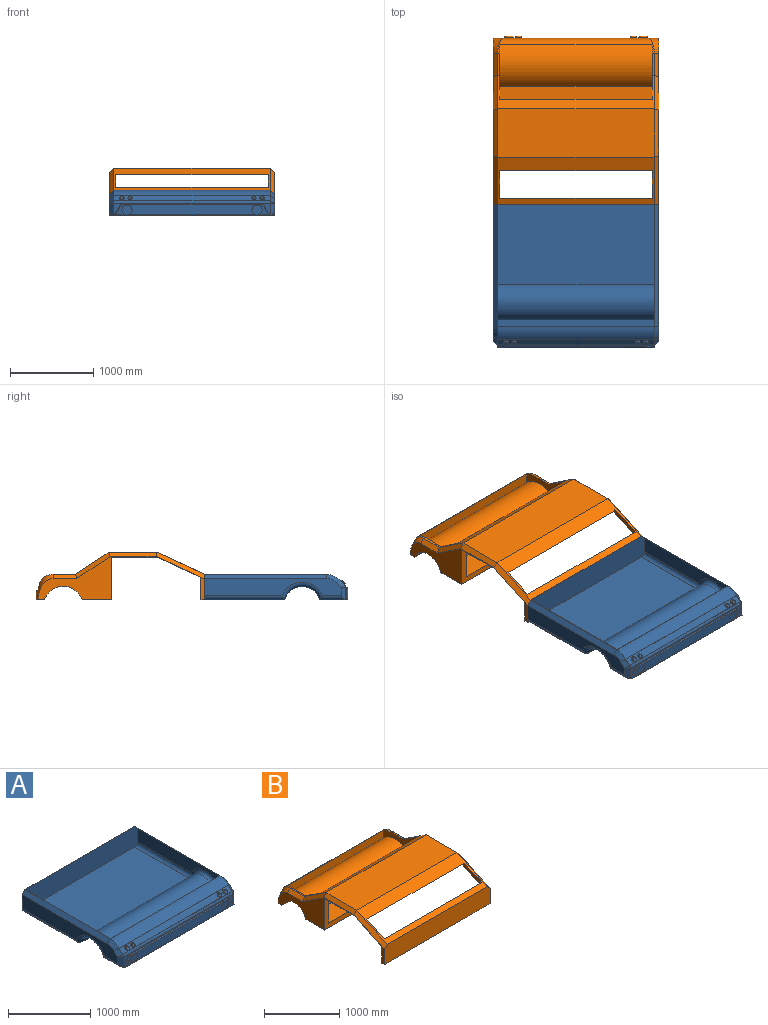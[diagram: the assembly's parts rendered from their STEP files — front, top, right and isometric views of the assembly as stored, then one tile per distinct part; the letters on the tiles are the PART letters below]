
ASSEMBLY  parts=2 mates=1
PART A: 79 faces, bbox 1981.2x1717.2x313 mm
  f0: plane 145.61x89.98mm, normal (0,-1,0), area 6551.4mm2, adj f11,f17,f63
  f1: plane 1879.6x327.04mm, normal (0,0,-1), area 614695.6mm2, adj f2,f22,f25,f63,f66,f74
  f2: cylinder r=215.54mm len=1879.6mm, axis (-1,0,0), area 1057523.4mm2, adj f1,f3,f23,f26
  f3: plane 1879.6x961.54mm, normal (0,0,-1), area 1807313.3mm2, adj f2,f4,f24,f27
  f4: plane 1981.2x306.36mm, normal (0,1,0), area 603262.1mm2, adj f3,f5,f7,f8,f16,f21,f24,f27
  f5: plane 1879.6x1462.7mm, normal (0,0,1), area 15264.3mm2, adj f4,f10,f16,f21,f32,f43,f48
  f6: plane 145.61x89.98mm, normal (0,-1,0), area 6551.4mm2, adj f11,f12,f66
  f7: plane 1641.03x204.76mm, normal (1,0,0), area 273561.9mm2, adj f4,f17,f19,f20,f21,f25,f26,f27
  f8: plane 1641.03x204.76mm, normal (-1,0,0), area 273561.9mm2, adj f4,f12,f14,f15,f16,f22,f23,f24
  f9: plane 1879.6x61.59mm, normal (0,-0.71,0.71), area 153947.2mm2, adj f10,f11,f14,f19,f55,f57,f59,f61
  f10: cylinder r=215.9mm len=1879.6mm, axis (-1,0,0), area 318719mm2, adj f5,f9,f15,f20,f28
  f11: cylinder r=50.8mm len=1879.6mm, axis (1,0,0), area 74992.7mm2, adj f0,f6,f9,f13,f18,f64
  f12: plane 145.61x50.8mm, normal (-0.71,-0.71,0), area 9677.9mm2, adj f6,f8,f13,f22
  f13: cone r=50.8mm half-angle=45deg, axis (1,0,0), area 1433.2mm2, adj f11,f12,f14
  f14: plane 97.51x97.51mm, normal (-0.71,-0.5,0.5), area 6257.1mm2, adj f8,f9,f13,f15
  f15: cone r=165.1mm half-angle=45deg, axis (1,0,0), area 10748.9mm2, adj f8,f10,f14,f16
  f16: plane 1462.7x50.8mm, normal (-0.71,0,0.71), area 105083.6mm2, adj f4,f5,f8,f15
  f17: plane 145.61x50.8mm, normal (0.71,-0.71,0), area 9677.9mm2, adj f0,f7,f18,f25
  f18: cone r=50.8mm half-angle=45deg, axis (-1,0,0), area 1433.2mm2, adj f11,f17,f19
  f19: plane 97.51x97.51mm, normal (0.71,-0.5,0.5), area 6257.1mm2, adj f7,f9,f18,f20
  f20: cone r=165.1mm half-angle=45deg, axis (-1,0,0), area 10748.9mm2, adj f7,f10,f19,f21
  f21: plane 1462.7x50.8mm, normal (0.71,0,0.71), area 105083.6mm2, adj f4,f5,f7,f20
  f22: cylinder r=50.8mm len=314.34mm, axis (0,1,0), area 21434.4mm2, adj f1,f8,f12,f23
  f23: torus R=266.34mm, axis (1,0,0), area 46455.3mm2, adj f2,f8,f22,f24
  f24: cylinder r=50.8mm len=961.54mm, axis (0,1,0), area 75659.8mm2, adj f3,f4,f8,f23
  f25: cylinder r=50.8mm len=314.34mm, axis (0,-1,0), area 21434.4mm2, adj f1,f7,f17,f26
  f26: torus R=266.34mm, axis (1,0,0), area 46455.3mm2, adj f2,f7,f25,f27
  f27: cylinder r=50.8mm len=961.54mm, axis (0,-1,0), area 75659.8mm2, adj f3,f4,f7,f26
  f28: plane 1877.5x2.54mm, normal (0,1,0), area 4762.4mm2, adj f10,f37,f43,f48
  f29: plane 1879.6x309.86mm, normal (0,0,1), area 582417.3mm2, adj f30,f33,f39,f44,f49,f52
  f30: cylinder r=218.08mm len=1879.6mm, axis (-1,0,0), area 1062679mm2, adj f29,f31,f50,f53
  f31: plane 1879.6x957.07mm, normal (0,0,1), area 1798907.1mm2, adj f30,f32,f51,f54
  f32: plane 1976.12x303.82mm, normal (0,-1,0), area 596686.5mm2, adj f5,f31,f34,f35,f43,f48,f51,f54
  f33: plane 1877.5x143.07mm, normal (0,1,0), area 268618.7mm2, adj f29,f38,f39,f44
  f34: plane 1637.44x203.7mm, normal (-1,0,0), area 271178.6mm2, adj f32,f44,f46,f47,f48,f52,f53,f54
  f35: plane 1637.44x203.7mm, normal (1,0,0), area 271178.6mm2, adj f32,f39,f41,f42,f43,f49,f50,f51
  f36: plane 1877.5x61.59mm, normal (0,0.71,-0.71), area 163520.3mm2, adj f37,f38,f41,f46
  f37: cylinder r=213.36mm len=1877.5mm, axis (-1,0,0), area 314616.8mm2, adj f28,f36,f42,f47
  f38: cylinder r=48.26mm len=1877.5mm, axis (1,0,0), area 71163.3mm2, adj f33,f36,f40,f45
  f39: plane 143.07x49.31mm, normal (0.71,0.71,0), area 9270.4mm2, adj f29,f33,f35,f40,f41,f49
  f40: cone r=49mm half-angle=45deg, axis (1,0,0), area 1293.4mm2, adj f38,f39,f41
  f41: plane 96.45x96.15mm, normal (0.71,0.5,-0.5), area 6073.5mm2, adj f35,f36,f39,f40,f42
  f42: cone r=163.3mm half-angle=45deg, axis (1,0,0), area 10335.7mm2, adj f35,f37,f41,f43
  f43: plane 1460.16x51.85mm, normal (0.71,0,-0.71), area 107073.7mm2, adj f5,f28,f32,f35,f42
  f44: plane 143.07x49.31mm, normal (-0.71,0.71,0), area 9270.4mm2, adj f29,f33,f34,f45,f46,f52
  f45: cone r=49mm half-angle=45deg, axis (-1,0,0), area 1293.4mm2, adj f38,f44,f46
  f46: plane 96.45x96.15mm, normal (-0.71,0.5,-0.5), area 6073.5mm2, adj f34,f36,f44,f45,f47
  f47: cone r=163.3mm half-angle=45deg, axis (-1,0,0), area 10335.7mm2, adj f34,f37,f46,f48
  f48: plane 1460.16x51.85mm, normal (-0.71,0,-0.71), area 107073.7mm2, adj f5,f28,f32,f34,f47
  f49: cylinder r=48.26mm len=308.81mm, axis (0,1,0), area 20122.9mm2, adj f29,f35,f39,f50
  f50: torus R=266.34mm, axis (1,0,0), area 44263.2mm2, adj f30,f35,f49,f51
  f51: cylinder r=48.26mm len=957.07mm, axis (0,1,0), area 71594.2mm2, adj f31,f32,f35,f50
  f52: cylinder r=48.26mm len=308.81mm, axis (0,-1,0), area 20122.9mm2, adj f29,f34,f44,f53
  f53: torus R=266.34mm, axis (1,0,0), area 44263.2mm2, adj f30,f34,f52,f54
  f54: cylinder r=48.26mm len=957.07mm, axis (0,-1,0), area 71594.2mm2, adj f31,f32,f34,f53
  f55: extruded ~65.11x59.14mm, area 2910mm2, adj f9,f78
  f56: plane 48.99x31.66mm, normal (0,-0.71,0.71), area 1713.6mm2, adj f78
  f57: extruded ~60.13x52.09mm, area 2563.7mm2, adj f9,f77
  f58: plane 41.94x26.68mm, normal (0,-0.71,0.71), area 1234.7mm2, adj f77
  f59: extruded ~60.13x52.09mm, area 2563.1mm2, adj f9,f76
  f60: plane 41.94x26.68mm, normal (0,-0.71,0.71), area 1234.7mm2, adj f76
  f61: extruded ~65.11x59.14mm, area 2910.3mm2, adj f9,f75
  f62: plane 48.99x31.66mm, normal (0,-0.71,0.71), area 1713.6mm2, adj f75
  f63: plane 145.61x89.98mm, normal (0.85,0,0.53), area 2173.9mm2, adj f0,f1,f64,f72
  f64: plane 1699.63x12.7mm, normal (0,0,1), area 21585.3mm2, adj f11,f63,f66,f71
  f65: cylinder r=60.65mm len=121.3mm, axis (0,1,0), area 4823.7mm2, adj f68,f69,f74
  f66: plane 145.61x89.98mm, normal (-0.85,0,0.53), area 2173.9mm2, adj f1,f6,f64,f73
  f67: cylinder r=60.65mm len=121.3mm, axis (0,1,0), area 4823.7mm2, adj f68,f70,f74
  f68: plane 1834.05x120.21mm, normal (0,-1,0), area 188673.1mm2, adj f65,f67,f71,f72,f73,f74
  f69: plane 121.3x121.3mm, normal (0,-1,0), area 11556.1mm2, adj f65
  f70: plane 121.3x121.3mm, normal (0,-1,0), area 11556.1mm2, adj f67
  f71: cylinder r=12.7mm len=1699.63mm, axis (1,0,0), area 33803.5mm2, adj f64,f68,f72,f73
  f72: cylinder r=12.7mm len=152.29mm, axis (0.53,0,-0.85), area 3198.3mm2, adj f63,f68,f71,f74
  f73: cylinder r=12.7mm len=152.29mm, axis (0.53,0,0.85), area 3198.3mm2, adj f66,f68,f71,f74
  f74: cylinder r=12.7mm len=1879.6mm, axis (-1,0,0), area 36923.4mm2, adj f1,f65,f67,f68,f72,f73
  f75: bspline ~60.43x43.93mm, area 1335.1mm2, adj f61,f62
  f76: bspline ~53.61x38.95mm, area 1157.9mm2, adj f59,f60
  f77: bspline ~53.67x38.95mm, area 1158.5mm2, adj f57,f58
  f78: bspline ~60.43x43.93mm, area 1335.1mm2, adj f55,f56
PART B: 50 faces, bbox 2232.6x2022.4x571.3 mm
  f0: plane 268.46x25.4mm, normal (0,0,1), area 6819mm2, adj f1,f26,f34,f36
  f1: plane 1879.6x402.51mm, normal (0,0.55,0.84), area 277933.2mm2, adj f0,f2,f14,f21,f25,f26,f29,f33
  f2: plane 268.46x25.4mm, normal (0,0,1), area 6819mm2, adj f1,f21,f30,f36
  f3: plane 1879.6x571.4mm, normal (0,-0.42,0.91), area 516873.4mm2, adj f4,f14,f17,f18,f19,f20,f27,f31
  f4: plane 1981.2x306.36mm, normal (0,-1,0), area 604105.8mm2, adj f3,f5,f15,f16,f27,f31
  f5: plane 1981.2x45.68mm, normal (0,0,-1), area 90495.3mm2, adj f4,f6,f15,f16
  f6: plane 1981.2x269.78mm, normal (0,1,0), area 534479.5mm2, adj f5,f7,f15,f16
  f7: plane 1981.2x520.86mm, normal (0,0.42,-0.91), area 219399.2mm2, adj f6,f8,f15,f16,f17,f18,f19,f20
  f8: plane 1981.2x555.42mm, normal (0,0,-1), area 1100392.4mm2, adj f7,f9,f15,f16
  f9: plane 1981.2x511.3mm, normal (0,-1,0), area 246879mm2, adj f8,f10,f15,f16,f21,f22,f25,f26
  f10: plane 1981.2x350.01mm, normal (0,0,-1), area 693440.1mm2, adj f9,f11,f15,f16
  f11: cylinder r=238.18mm len=1981.2mm, axis (-1,0,0), area 1170877.9mm2, adj f10,f12,f15,f16
  f12: plane 1981.2x74.38mm, normal (0,0,-1), area 147356.3mm2, adj f11,f13,f15,f16
  f13: plane 1981.2x128.56mm, normal (0,1,0), area 214744.8mm2, adj f12,f15,f16,f35,f36,f37,f38,f40
  f14: plane 1879.6x576.81mm, normal (0,0,1), area 1084167.8mm2, adj f1,f3,f28,f32
  f15: plane 1996.98x520.51mm, normal (1,0,0), area 235180.7mm2, adj f4,f5,f6,f7,f8,f9,f10,f11
  f16: plane 1996.98x520.51mm, normal (-1,0,0), area 235180.7mm2, adj f4,f5,f6,f7,f8,f9,f10,f11
  f17: plane 455.43x211.18mm, normal (1,0,0), area 22708mm2, adj f3,f7,f18,f20
  f18: plane 1828.8x57.76mm, normal (0,1,0), area 105630.1mm2, adj f3,f7,f17,f19
  f19: plane 455.43x211.18mm, normal (-1,0,0), area 22708mm2, adj f3,f7,f18,f20
  f20: plane 1828.8x124.56mm, normal (0,0,-1), area 227803.1mm2, adj f3,f7,f17,f19
  f21: plane 798.83x418.91mm, normal (1,0,0), area 175801.9mm2, adj f1,f2,f9,f22,f23,f24,f25,f36
  f22: plane 1828.8x300.92mm, normal (0,0,1), area 550325.3mm2, adj f9,f21,f23,f26
  f23: cylinder r=314.38mm len=1828.8mm, axis (-1,0,0), area 1064670.2mm2, adj f21,f22,f24,f26
  f24: plane 1828.8x130.58mm, normal (0,-1,0), area 238811.4mm2, adj f21,f23,f26,f36
  f25: plane 1828.8x142.01mm, normal (0,0,-1), area 259712.3mm2, adj f1,f9,f21,f26
  f26: plane 798.83x418.91mm, normal (-1,0,0), area 175801.9mm2, adj f0,f1,f9,f22,f23,f24,f25,f36
  f27: plane 582.61x320.95mm, normal (-0.71,-0.3,0.64), area 45692.7mm2, adj f3,f4,f16,f28
  f28: plane 576.81x50.8mm, normal (-0.71,0,0.71), area 40489.9mm2, adj f14,f16,f27,f29
  f29: plane 417.73x315.75mm, normal (-0.71,0.39,0.59), area 34619.8mm2, adj f1,f16,f28,f30
  f30: plane 283.68x50.8mm, normal (-0.71,0,0.71), area 19833.6mm2, adj f2,f16,f29,f37
  f31: plane 582.61x320.95mm, normal (0.71,-0.3,0.64), area 45692.7mm2, adj f3,f4,f15,f32
  f32: plane 576.81x50.8mm, normal (0.71,0,0.71), area 40489.9mm2, adj f14,f15,f31,f33
  f33: plane 417.73x315.75mm, normal (0.71,0.39,0.59), area 34619.8mm2, adj f1,f15,f32,f34
  f34: plane 283.68x50.8mm, normal (0.71,0,0.71), area 19833.6mm2, adj f0,f15,f33,f35
  f35: cylinder r=177.8mm len=302.25mm, axis (-0.71,0,0.71), area 30634.8mm2, adj f13,f15,f34,f36
  f36: cylinder r=177.8mm len=1879.6mm, axis (-1,0,0), area 312222.9mm2, adj f0,f2,f13,f21,f24,f26,f35,f37
  f37: cylinder r=177.8mm len=302.25mm, axis (0.71,0,0.71), area 30634.8mm2, adj f13,f16,f30,f36
  f38: cylinder r=53mm len=106mm, axis (0,-1,0), area 4229.3mm2, adj f13,f49
  f39: plane 80.6x80.6mm, normal (0,1,0), area 5102.5mm2, adj f49
  f40: cylinder r=32.92mm len=65.85mm, axis (0,-1,0), area 2627.2mm2, adj f13,f48
  f41: plane 40.45x40.45mm, normal (0,1,0), area 1284.9mm2, adj f48
  f42: cylinder r=32.92mm len=65.85mm, axis (0,-1,0), area 2627.2mm2, adj f13,f47
  f43: plane 40.45x40.45mm, normal (0,1,0), area 1284.9mm2, adj f47
  f44: cylinder r=53mm len=106mm, axis (0,-1,0), area 4229.3mm2, adj f13,f46
  f45: plane 80.6x80.6mm, normal (0,1,0), area 5102.5mm2, adj f46
  f46: torus R=40.3mm, axis (0,1,0), area 6064.9mm2, adj f44,f45
  f47: torus R=20.22mm, axis (0,1,0), area 3548.4mm2, adj f42,f43
  f48: torus R=20.22mm, axis (0,1,0), area 3548.4mm2, adj f40,f41
  f49: torus R=40.3mm, axis (0,1,0), area 6064.9mm2, adj f38,f39
PLACE A t=(0,451.23,41.92)mm
PLACE B at identity
MATE fastened A.f4 <-> B.f4  axis (0,1,0) through (990.6,910.64,10.08)mm
